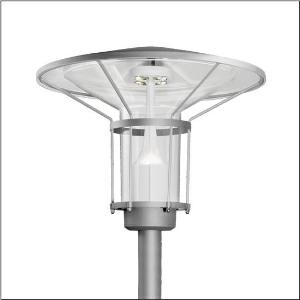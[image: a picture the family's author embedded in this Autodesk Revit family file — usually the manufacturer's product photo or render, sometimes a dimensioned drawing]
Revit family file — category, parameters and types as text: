
# Revit family: laterne_classic_iq___p1_0a_5xa5245ff14h000022_892e
name_source: partatom
category: Lighting Fixtures
units: mm (PartAtom-declared; Revit-internal decimal feet)

## family parameters
Cut with Voids When Loaded = No
Host = Face
Light Source = No
Part Type = Normal
Room Calculation Point = No
Round Connector Dimension = Use Diameter
Shared = No

## types (1)
- --- (1 x LED, 1360 lm, 10.5 W, 3000K)
    Apparent Load = 11 VA
    CIE Flux Codes = 30 61 91 96 100
    Color Rendering = 70
    Color Temperature = 3000K
    Default Elevation = 1800 mm
    Description = Lantern Classic iQ, mast luminaire, Module 540 iQ-SR, primary light control with 3 zone facetted reflector, of plastic, silver coated, highly specular, structured, primary optical cover: cover, of PMMA, transparent, light distribution: P1.0a, light emission: direct distribution, primary light characteristic: strongly asymmetric, installation type: post-top, LED, High Power LED, rated luminous flux: 1.360lm, luminous efficacy: 130lm/W, light colour: 730, colour temperature: 3000K, control gear: ECG iQ, control: Street-Remote, Auto-Match, Temp-Guard, Lumen-Switch, Night-Set, Smart-Wire, Light-Fading, Desk-Remote (wireless, voltage-free reading and setting of iQ features in the workshop via application-optimized NFC function/RFID function), optimised constant luminous flux control (CLO 2.0), presetting dimming logarithmic, mains connection: 230..240V, AC, 50/60Hz, connection cable pre-assembled, cable length: 5,5m, wiring characteristics: H07RN-F, start of lifetime: 11W, end of service life: 11W, reduction: 5W, luminaire housing, upper part, of glass-fibre reinforced polyester, coated, Siteco® metallic grey (DB 702S), diameter: 750mm, height: 596mm, spigot size: d x l = 76 x 70mm (post-top) | with reducer (optional accessory) 60 x 70mm, post-top mast mounting element, of diecast aluminium, coated, Siteco® metallic grey (DB 702S), Module 540 iQ-SR, traffic white (RAL 9016), equipment: standard, protection rating (complete): IP65, insulation class (complete): insulation class II (safety insulation), certification: CE, ENEC, VDE, packaging unit: 1 piece

Light Distribution: P1.0a
    Height = 596 mm
    Lamp = 1 x LED
    Lamp Light Flux = 1360 lm
    Lamp Power = 10.5 W
    Lamp count = 1
    Length = 750 mm
    Luminous efficacy = 130 lm/W
    Manufacturer = Siteco
    ModVariant = No
    Model = 5XA5245FF14H000022
    Number of Poles = 1
    OnlyDefault = Yes
    Power Factor = 1
    Product Name = Laterne Classic iQ | P1.0a
    Product group = mast luminaire | pylon top
    ProductGroupID = 6100
    Protection Class = Protection class II
    Protection Degree = IP 65
    RLX_Detail_Level = 1
    RLX_Emergency_Light_Flux = 0 lm
    RLX_Emergency_Type = 0
    RLX_Emergency_Type_DB = No
    RlxData = <blob elided: 64677 chars, md5=bcb742a5>
    Socket = socket
    Standby Power = 0 W
    System Light Flux = 1360 lm
    System Power = 11 W
    Type Comments = factory setting: luminous flux: 100 % | dim-lin: 254 | 419 mA
    Type Image = l_1006052.jpg
    URL = http://relux.com
    VarID = @adj_110357
    Voltage = 0 V
    Weight = 0.00 kg
    Width = 0 mm  [stored 0 ft]

note: [stored X ft] marks values corroborated as IEEE doubles in the binary element streams (Revit-internal decimal feet)

## geometry (parser evidence)
native form markers: Blend x4, Sweep x11
no freeform markers — native parametric forms only
